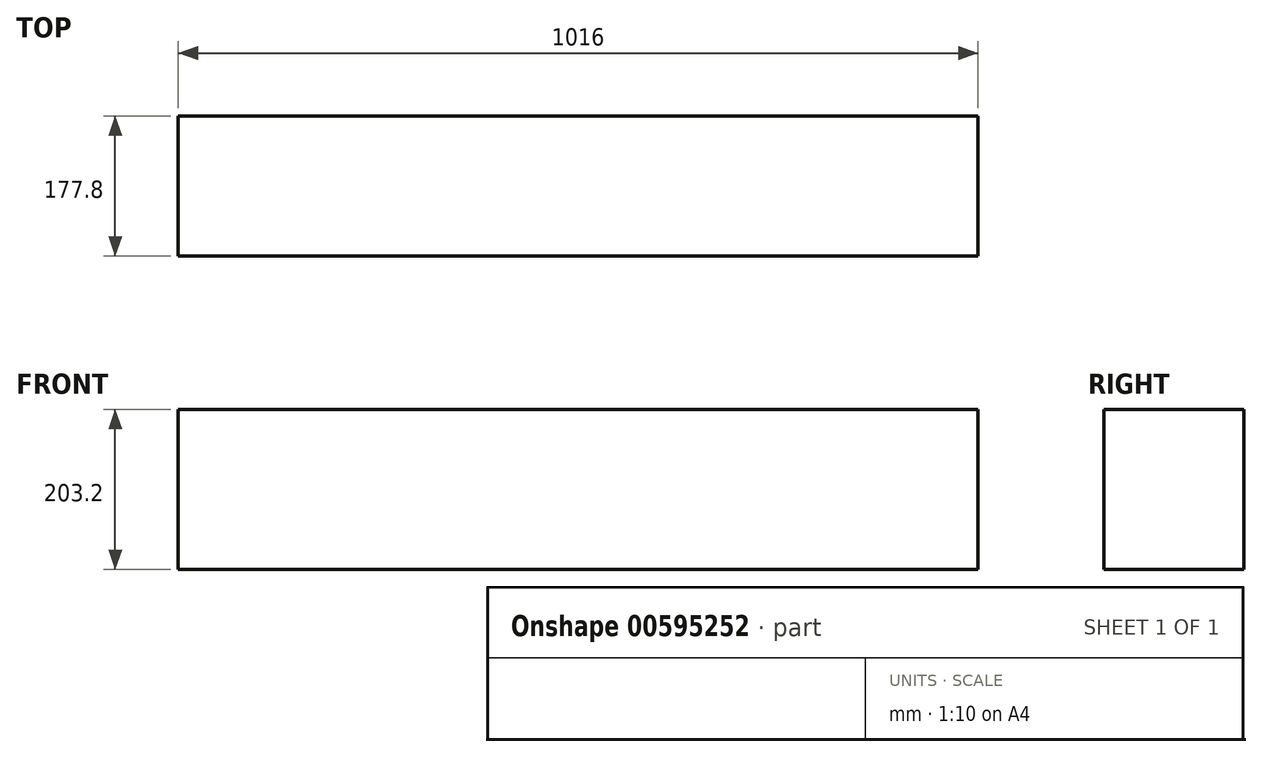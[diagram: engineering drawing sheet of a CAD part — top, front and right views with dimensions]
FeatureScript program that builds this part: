
annotation { "Feature Type Name" : "Feature", "Feature Type Description" : "" }
export const myFeature = defineFeature(function(context is Context, id is Id, definition is map)
    precondition{}
    {
        {
            var Q0;
            Q0=qCreatedBy(makeId("Front.planeOp"),FACE);
            var sketch = newSketch(context, id + "F0", { "sketchPlane" : qUnion([Q0])});
            skLineSegment(sketch, "E0.bottom", {"start": v(508, -101.6) * mm, "end": v(-508, -101.6) * mm});
            skLineSegment(sketch, "E0.top", {"start": v(508, 101.6) * mm, "end": v(-508, 101.6) * mm});
            skLineSegment(sketch, "E0.left", {"start": v(508, -101.6) * mm, "end": v(508, 101.6) * mm});
            skLineSegment(sketch, "E0.right", {"start": v(-508, -101.6) * mm, "end": v(-508, 101.6) * mm});
            skPoint(sketch, "E0.middle", {"position": v(0, 0) * mm});
            skSolve(sketch);
        }
        {
            var Q0;
            Q0=makeQuery(id+"F0.imprint","IMPRINT",FACE,{"disambiguationData":[TD([[makeQuery(id+"F0.imprint","IMPRINT",EDGE,{"derivedFrom":sQuery(id+"F0.wireOp",EDGE,"E0.bottom")}),-1.0]])]});
            extrude(context, id + "F1", {"entities" : qUnion([Q0]), "depth" : 177.8 * mm, "offsetDistance" : 25.4 * mm});
        }
    });
